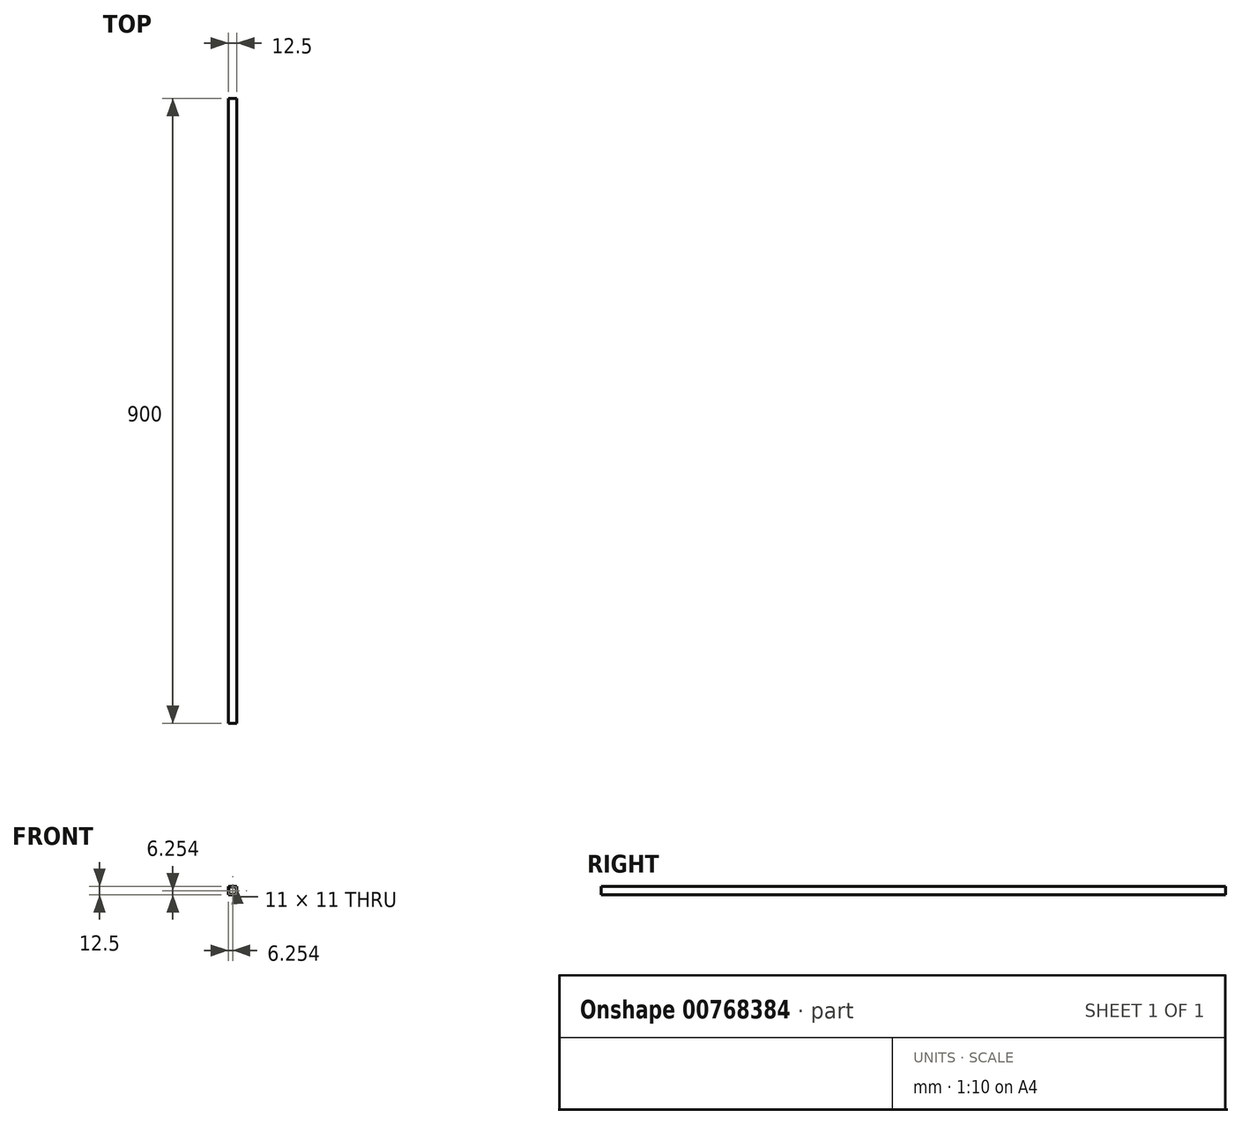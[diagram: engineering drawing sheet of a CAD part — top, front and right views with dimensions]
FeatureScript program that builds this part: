
annotation { "Feature Type Name" : "Feature", "Feature Type Description" : "" }
export const myFeature = defineFeature(function(context is Context, id is Id, definition is map)
    precondition{}
    {
        {
            var Q0;
            Q0=qCreatedBy(makeId("Front.planeOp"),FACE);
            var sketch = newSketch(context, id + "F0", { "sketchPlane" : qUnion([Q0])});
            skLineSegment(sketch, "E0.bottom", {"start": v(-118.89, 45.33) * mm, "end": v(-106.39, 45.33) * mm});
            skLineSegment(sketch, "E0.top", {"start": v(-118.89, 32.83) * mm, "end": v(-106.39, 32.83) * mm});
            skLineSegment(sketch, "E0.left", {"start": v(-118.89, 45.33) * mm, "end": v(-118.89, 32.83) * mm});
            skLineSegment(sketch, "E0.right", {"start": v(-106.39, 45.33) * mm, "end": v(-106.39, 32.83) * mm});
            skLineSegment(sketch, "E1.bottom", {"start": v(-118.14, 44.58) * mm, "end": v(-107.14, 44.58) * mm});
            skLineSegment(sketch, "E1.top", {"start": v(-118.14, 33.58) * mm, "end": v(-107.14, 33.58) * mm});
            skLineSegment(sketch, "E1.left", {"start": v(-118.14, 44.58) * mm, "end": v(-118.14, 33.58) * mm});
            skLineSegment(sketch, "E1.right", {"start": v(-107.14, 44.58) * mm, "end": v(-107.14, 33.58) * mm});
            skSolve(sketch);
        }
        {
            var Q0;
            Q0=makeQuery(id+"F0.imprint","IMPRINT",FACE,{"disambiguationData":[TD([[makeQuery(id+"F0.imprint","IMPRINT",EDGE,{"derivedFrom":sQuery(id+"F0.wireOp",EDGE,"E0.bottom")}),-1.0]])]});
            extrude(context, id + "F1", {"entities" : qUnion([Q0]), "depth" : 900 * mm, "offsetDistance" : 25 * mm});
        }
    });
